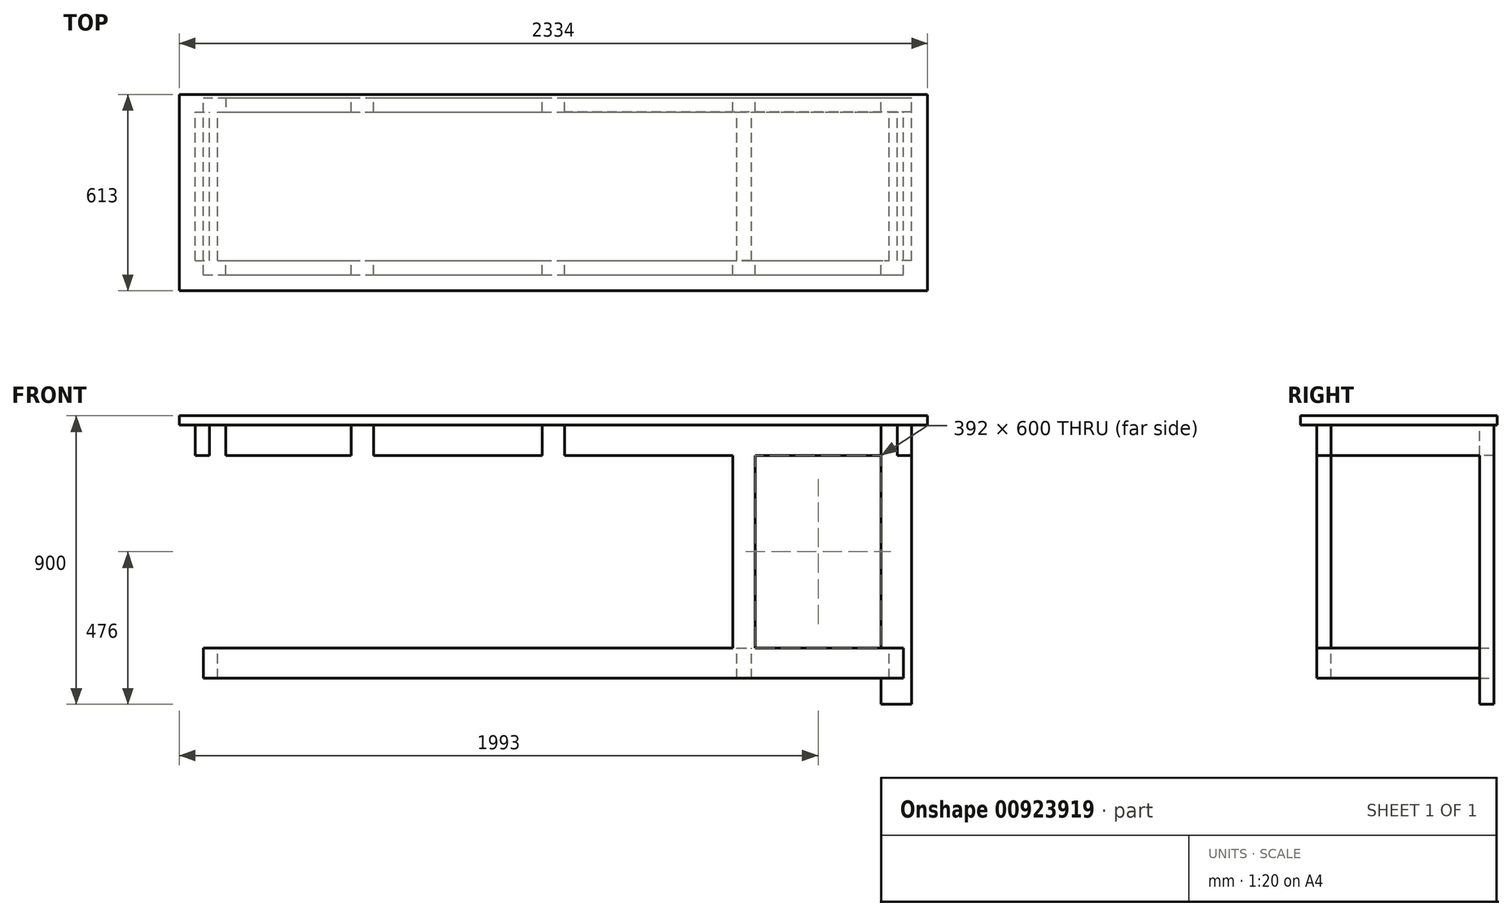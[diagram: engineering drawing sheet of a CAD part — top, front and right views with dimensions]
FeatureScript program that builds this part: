
annotation { "Feature Type Name" : "Feature", "Feature Type Description" : "" }
export const myFeature = defineFeature(function(context is Context, id is Id, definition is map)
    precondition{}
    {
        {
            var Q0;
            Q0=qCreatedBy(makeId("Top.planeOp"),FACE);
            cPlane(context, id + "F0", {"entities" : qUnion([Q0]), "cplaneType" : CPlaneType.OFFSET, "offset" : 900 * mm, "width" : 150 * mm, "height" : 150 * mm});
        }
        {
            var Q0;
            Q0=qCreatedBy(id+"F0.planeOp",FACE);
            var sketch = newSketch(context, id + "F1", { "sketchPlane" : qUnion([Q0])});
            skLineSegment(sketch, "E0.bottom", {"start": v(1167, -306.5) * mm, "end": v(-1167, -306.5) * mm});
            skLineSegment(sketch, "E0.top", {"start": v(1167, 306.5) * mm, "end": v(-1167, 306.5) * mm});
            skLineSegment(sketch, "E0.left", {"start": v(1167, -306.5) * mm, "end": v(1167, 306.5) * mm});
            skLineSegment(sketch, "E0.right", {"start": v(-1167, -306.5) * mm, "end": v(-1167, 306.5) * mm});
            skPoint(sketch, "E0.middle", {"position": v(0, 0) * mm});
            skSolve(sketch);
        }
        {
            var Q0;
            Q0=makeQuery(id+"F1.imprint","IMPRINT",FACE,{"disambiguationData":[TD([[makeQuery(id+"F1.imprint","IMPRINT",EDGE,{"derivedFrom":sQuery(id+"F1.wireOp",EDGE,"E0.bottom")}),-1.0]])]});
            extrude(context, id + "F2", {"entities" : qUnion([Q0]), "oppositeDirection" : true, "depth" : 29 * mm, "offsetDistance" : 25 * mm});
        }
        {
            var Q0;
            Q0=makeQuery(id+"F2.opExtrude","CAP_FACE",FACE,{"disambiguationData":[OSD([sQuery(id+"F1.wireOp",EDGE,"E0.bottom"),sQuery(id+"F1.wireOp",EDGE,"E0.top"),sQuery(id+"F1.wireOp",EDGE,"E0.left"),sQuery(id+"F1.wireOp",EDGE,"E0.right")])],"isStart":false});
            var sketch = newSketch(context, id + "F3", { "sketchPlane" : qUnion([Q0])});
            skLineSegment(sketch, "E1", {"start": v(0, -352.14) * mm, "end": v(0, 338.4) * mm, "construction": true});
            skPoint(sketch, "E1.endSnap0", {"position": v(0, 306.5) * mm});
            skLineSegment(sketch, "E2", {"start": v(-1212.18, 0) * mm, "end": v(1197.3, 0) * mm, "construction": true});
            skLineSegment(sketch, "E3.bottom", {"start": v(-1117, 256.5) * mm, "end": v(1117, 256.5) * mm});
            skLineSegment(sketch, "E3.top", {"start": v(-1117, -296.5) * mm, "end": v(1117, -296.5) * mm});
            skLineSegment(sketch, "E3.left", {"start": v(-1117, 256.5) * mm, "end": v(-1117, -296.5) * mm});
            skLineSegment(sketch, "E3.right", {"start": v(1117, 256.5) * mm, "end": v(1117, -296.5) * mm});
            skLineSegment(sketch, "E4.bottom", {"start": v(-1072, 211.5) * mm, "end": v(1072, 211.5) * mm});
            skLineSegment(sketch, "E4.top", {"start": v(-1072, -251.5) * mm, "end": v(1072, -251.5) * mm});
            skLineSegment(sketch, "E4.left", {"start": v(-1072, 211.5) * mm, "end": v(-1072, -251.5) * mm});
            skLineSegment(sketch, "E4.right", {"start": v(1072, 211.5) * mm, "end": v(1072, -251.5) * mm});
            skLineSegment(sketch, "E5.bottom", {"start": v(-22.5, 211.5) * mm, "end": v(22.5, 211.5) * mm});
            skLineSegment(sketch, "E5.top", {"start": v(-22.5, -251.5) * mm, "end": v(22.5, -251.5) * mm});
            skLineSegment(sketch, "E5.left", {"start": v(-22.5, 211.5) * mm, "end": v(-22.5, -251.5) * mm});
            skLineSegment(sketch, "E5.right", {"start": v(22.5, 211.5) * mm, "end": v(22.5, -251.5) * mm});
            skLineSegment(sketch, "E6.bottom", {"start": v(-1117, 256.5) * mm, "end": v(-1022, 256.5) * mm});
            skLineSegment(sketch, "E6.top", {"start": v(-1117, 211.5) * mm, "end": v(-1022, 211.5) * mm});
            skLineSegment(sketch, "E6.left", {"start": v(-1117, 256.5) * mm, "end": v(-1117, 211.5) * mm});
            skLineSegment(sketch, "E6.right", {"start": v(-1022, 256.5) * mm, "end": v(-1022, 211.5) * mm});
            skLineSegment(sketch, "E7.bottom", {"start": v(-35, 256.5) * mm, "end": v(35, 256.5) * mm});
            skLineSegment(sketch, "E7.top", {"start": v(-35, 211.5) * mm, "end": v(35, 211.5) * mm});
            skLineSegment(sketch, "E7.left", {"start": v(-35, 256.5) * mm, "end": v(-35, 211.5) * mm});
            skLineSegment(sketch, "E7.right", {"start": v(35, 256.5) * mm, "end": v(35, 211.5) * mm});
            skLineSegment(sketch, "E8.bottom", {"start": v(-1117, -296.5) * mm, "end": v(-1022, -296.5) * mm});
            skLineSegment(sketch, "E8.top", {"start": v(-1117, -251.5) * mm, "end": v(-1022, -251.5) * mm});
            skLineSegment(sketch, "E8.left", {"start": v(-1117, -296.5) * mm, "end": v(-1117, -251.5) * mm});
            skLineSegment(sketch, "E8.right", {"start": v(-1022, -296.5) * mm, "end": v(-1022, -251.5) * mm});
            skLineSegment(sketch, "E9.MirrorCS", {"start": v(1022, -296.5) * mm, "end": v(1022, -251.5) * mm});
            skLineSegment(sketch, "E10.MirrorCS", {"start": v(1117, -251.5) * mm, "end": v(1022, -251.5) * mm});
            skLineSegment(sketch, "E11.MirrorCS", {"start": v(1117, -296.5) * mm, "end": v(1022, -296.5) * mm});
            skLineSegment(sketch, "E12.MirrorCS", {"start": v(1117, 211.5) * mm, "end": v(1022, 211.5) * mm});
            skLineSegment(sketch, "E13.MirrorCS", {"start": v(1117, 256.5) * mm, "end": v(1022, 256.5) * mm});
            skLineSegment(sketch, "E14.MirrorCS", {"start": v(1022, 256.5) * mm, "end": v(1022, 211.5) * mm});
            skLineSegment(sketch, "E15.MirrorCS", {"start": v(1117, 256.5) * mm, "end": v(1117, 211.5) * mm});
            skLineSegment(sketch, "E16.bottom", {"start": v(-35, -251.5) * mm, "end": v(35, -251.5) * mm});
            skLineSegment(sketch, "E16.top", {"start": v(-35, -296.5) * mm, "end": v(35, -296.5) * mm});
            skLineSegment(sketch, "E16.left", {"start": v(-35, -251.5) * mm, "end": v(-35, -296.5) * mm});
            skLineSegment(sketch, "E16.right", {"start": v(35, -251.5) * mm, "end": v(35, -296.5) * mm});
            skLineSegment(sketch, "E17.bottom", {"start": v(-630, 256.5) * mm, "end": v(-560, 256.5) * mm});
            skLineSegment(sketch, "E17.top", {"start": v(-630, 211.5) * mm, "end": v(-560, 211.5) * mm});
            skLineSegment(sketch, "E17.left", {"start": v(-630, 256.5) * mm, "end": v(-630, 211.5) * mm});
            skLineSegment(sketch, "E17.right", {"start": v(-560, 256.5) * mm, "end": v(-560, 211.5) * mm});
            skLineSegment(sketch, "E18.bottom", {"start": v(-630, -251.5) * mm, "end": v(-560, -251.5) * mm});
            skLineSegment(sketch, "E18.top", {"start": v(-630, -296.5) * mm, "end": v(-560, -296.5) * mm});
            skLineSegment(sketch, "E18.left", {"start": v(-630, -251.5) * mm, "end": v(-630, -296.5) * mm});
            skLineSegment(sketch, "E18.right", {"start": v(-560, -251.5) * mm, "end": v(-560, -296.5) * mm});
            skLineSegment(sketch, "E19.MirrorCS", {"start": v(630, 256.5) * mm, "end": v(630, 211.5) * mm});
            skLineSegment(sketch, "E20.MirrorCS", {"start": v(630, 256.5) * mm, "end": v(560, 256.5) * mm});
            skLineSegment(sketch, "E21.MirrorCS", {"start": v(560, 256.5) * mm, "end": v(560, 211.5) * mm});
            skLineSegment(sketch, "E22.MirrorCS", {"start": v(630, 211.5) * mm, "end": v(560, 211.5) * mm});
            skLineSegment(sketch, "E23.MirrorCS", {"start": v(630, -251.5) * mm, "end": v(630, -296.5) * mm});
            skLineSegment(sketch, "E24.MirrorCS", {"start": v(630, -296.5) * mm, "end": v(560, -296.5) * mm});
            skLineSegment(sketch, "E25.MirrorCS", {"start": v(560, -251.5) * mm, "end": v(560, -296.5) * mm});
            skSolve(sketch);
        }
        {
            var Q0;
            Q0=makeQuery(id+"F3.imprint","IMPRINT",FACE,{"disambiguationData":[TD([[makeQuery(id+"F3.imprint","IMPRINT",EDGE,{"derivedFrom":sQuery(id+"F3.wireOp",EDGE,"E6.bottom")}),-1.0]])]});
            var Q1;
            Q1=makeQuery(id+"F3.imprint","IMPRINT",FACE,{"disambiguationData":[TD([[makeQuery(id+"F3.imprint","IMPRINT",EDGE,{"derivedFrom":sQuery(id+"F3.wireOp",EDGE,"E8.bottom")}),1.0]])]});
            var Q2;
            {var subQ1=sQuery(id+"F3.wireOp",EDGE,"E9.MirrorCS");Q2=makeQuery(id+"F3.imprint","IMPRINT",FACE,{"disambiguationData":[TD([[makeQuery(id+"F3.imprint","IMPRINT",EDGE,{"derivedFrom":subQ1}),-1.0]])]});}
            var Q3;
            Q3=makeQuery(id+"F3.imprint","IMPRINT",FACE,{"disambiguationData":[TD([[makeQuery(id+"F3.imprint","IMPRINT",EDGE,{"derivedFrom":sQuery(id+"F3.wireOp",EDGE,"E13.MirrorCS")}),1.0]])]});
            var Q4;
            Q4=makeQuery(id+"F3.imprint","IMPRINT",FACE,{"disambiguationData":[TD([[makeQuery(id+"F3.imprint","IMPRINT",EDGE,{"derivedFrom":sQuery(id+"F3.wireOp",EDGE,"E7.bottom")}),-1.0]])]});
            var Q5;
            Q5=makeQuery(id+"F3.imprint","IMPRINT",FACE,{"disambiguationData":[TD([[makeQuery(id+"F3.imprint","IMPRINT",EDGE,{"derivedFrom":sQuery(id+"F3.wireOp",EDGE,"E16.top")}),1.0]])]});
            extrude(context, id + "F4", {"entities" : qUnion([Q0, Q1, Q2, Q3, Q4, Q5]), "operationType" : NewBodyOperationType.ADD, "depth" : (900 - 29) * mm, "offsetDistance" : 25 * mm});
        }
        {
            var Q0;
            Q0=qCreatedBy(makeId("Top.planeOp"),FACE);
            cPlane(context, id + "F5", {"entities" : qUnion([Q0]), "cplaneType" : CPlaneType.OFFSET, "offset" : 176 * mm, "width" : 150 * mm, "height" : 150 * mm});
        }
        {
            var Q0;
            Q0=qCreatedBy(id+"F5.planeOp",FACE);
            var sketch = newSketch(context, id + "F6", { "sketchPlane" : qUnion([Q0])});
            skLineSegment(sketch, "E26", {"start": v(0, -296.69) * mm, "end": v(0, 323.31) * mm, "construction": true});
            skLineSegment(sketch, "E27", {"start": v(-1009.8, 0) * mm, "end": v(1031.2, 0) * mm, "construction": true});
            skLineSegment(sketch, "E28.bottom", {"start": v(-1092, -256.5) * mm, "end": v(1092, -256.5) * mm});
            skLineSegment(sketch, "E28.top", {"start": v(-1092, 296.5) * mm, "end": v(1092, 296.5) * mm});
            skLineSegment(sketch, "E28.left", {"start": v(-1092, -256.5) * mm, "end": v(-1092, 296.5) * mm});
            skLineSegment(sketch, "E28.right", {"start": v(1092, -256.5) * mm, "end": v(1092, 296.5) * mm});
            skLineSegment(sketch, "E29.bottom", {"start": v(-1047, -211.5) * mm, "end": v(1047, -211.5) * mm});
            skLineSegment(sketch, "E29.top", {"start": v(-1047, 251.5) * mm, "end": v(1047, 251.5) * mm});
            skLineSegment(sketch, "E29.left", {"start": v(-1047, -211.5) * mm, "end": v(-1047, 251.5) * mm});
            skLineSegment(sketch, "E29.right", {"start": v(1047, -211.5) * mm, "end": v(1047, 251.5) * mm});
            skLineSegment(sketch, "E30.bottom", {"start": v(-22.5, -211.5) * mm, "end": v(22.5, -211.5) * mm});
            skLineSegment(sketch, "E30.top", {"start": v(-22.5, 251.5) * mm, "end": v(22.5, 251.5) * mm});
            skLineSegment(sketch, "E30.left", {"start": v(-22.5, -211.5) * mm, "end": v(-22.5, 251.5) * mm});
            skLineSegment(sketch, "E30.right", {"start": v(22.5, -211.5) * mm, "end": v(22.5, 251.5) * mm});
            skLineSegment(sketch, "E31.bottom", {"start": v(-617.5, -211.5) * mm, "end": v(-572.5, -211.5) * mm});
            skLineSegment(sketch, "E31.top", {"start": v(-617.5, 251.5) * mm, "end": v(-572.5, 251.5) * mm});
            skLineSegment(sketch, "E31.left", {"start": v(-617.5, -211.5) * mm, "end": v(-617.5, 251.5) * mm});
            skLineSegment(sketch, "E31.right", {"start": v(-572.5, -211.5) * mm, "end": v(-572.5, 251.5) * mm});
            skLineSegment(sketch, "E32.MirrorCS", {"start": v(572.5, -211.5) * mm, "end": v(572.5, 251.5) * mm});
            skLineSegment(sketch, "E33.MirrorCS", {"start": v(617.5, -211.5) * mm, "end": v(617.5, 251.5) * mm});
            skLineSegment(sketch, "E34.MirrorCS", {"start": v(617.5, 251.5) * mm, "end": v(572.5, 251.5) * mm});
            skSolve(sketch);
        }
        {
            var Q0;
            {var subQ0=sQuery(id+"F3.wireOp",EDGE,"E3.left");Q0=makeQuery(id+"F3.imprint","IMPRINT",FACE,{"disambiguationData":[TD([[makeQuery(id+"F3.imprint","IMPRINT",EDGE,{"derivedFrom":subQ0}),1.0]])]});}
            var Q1;
            {var subQ0=sQuery(id+"F3.wireOp",EDGE,"E6.right");Q1=makeQuery(id+"F3.imprint","IMPRINT",FACE,{"disambiguationData":[TD([[makeQuery(id+"F3.imprint","IMPRINT",EDGE,{"derivedFrom":subQ0}),1.0]])]});}
            var Q2;
            {var subQ0=sQuery(id+"F3.wireOp",EDGE,"E8.right");Q2=makeQuery(id+"F3.imprint","IMPRINT",FACE,{"disambiguationData":[TD([[makeQuery(id+"F3.imprint","IMPRINT",EDGE,{"derivedFrom":subQ0}),-1.0]])]});}
            var Q3;
            {var subQ0=sQuery(id+"F3.wireOp",EDGE,"E16.left");Q3=makeQuery(id+"F3.imprint","IMPRINT",FACE,{"disambiguationData":[TD([[makeQuery(id+"F3.imprint","IMPRINT",EDGE,{"derivedFrom":subQ0}),-1.0]])]});}
            var Q4;
            {var subQ0=sQuery(id+"F3.wireOp",EDGE,"E7.left");Q4=makeQuery(id+"F3.imprint","IMPRINT",FACE,{"disambiguationData":[TD([[makeQuery(id+"F3.imprint","IMPRINT",EDGE,{"derivedFrom":subQ0}),-1.0]])]});}
            var Q5;
            {var subQ0=sQuery(id+"F3.wireOp",EDGE,"E7.right");Q5=makeQuery(id+"F3.imprint","IMPRINT",FACE,{"disambiguationData":[TD([[makeQuery(id+"F3.imprint","IMPRINT",EDGE,{"derivedFrom":subQ0}),1.0]])]});}
            var Q6;
            {var subQ0=sQuery(id+"F3.wireOp",EDGE,"E16.right");Q6=makeQuery(id+"F3.imprint","IMPRINT",FACE,{"disambiguationData":[TD([[makeQuery(id+"F3.imprint","IMPRINT",EDGE,{"derivedFrom":subQ0}),1.0]])]});}
            var Q7;
            {var subQ0=sQuery(id+"F3.wireOp",EDGE,"E9.MirrorCS");Q7=makeQuery(id+"F3.imprint","IMPRINT",FACE,{"disambiguationData":[TD([[makeQuery(id+"F3.imprint","IMPRINT",EDGE,{"derivedFrom":subQ0}),1.0]])]});}
            var Q8;
            {var subQ0=sQuery(id+"F3.wireOp",EDGE,"E14.MirrorCS");Q8=makeQuery(id+"F3.imprint","IMPRINT",FACE,{"disambiguationData":[TD([[makeQuery(id+"F3.imprint","IMPRINT",EDGE,{"derivedFrom":subQ0}),-1.0]])]});}
            var Q9;
            {var subQ5=sQuery(id+"F3.wireOp",EDGE,"E4.right");Q9=makeQuery(id+"F3.imprint","IMPRINT",FACE,{"disambiguationData":[TD([[makeQuery(id+"F3.imprint","IMPRINT",EDGE,{"derivedFrom":subQ5}),1.0]])]});}
            extrude(context, id + "F7", {"entities" : qUnion([Q0, Q1, Q2, Q3, Q4, Q5, Q6, Q7, Q8, Q9]), "operationType" : NewBodyOperationType.ADD, "depth" : 95 * mm, "offsetDistance" : 25 * mm});
        }
        {
            var Q0;
            Q0=makeQuery(id+"F3.imprint","IMPRINT",FACE,{"disambiguationData":[TD([[makeQuery(id+"F3.imprint","IMPRINT",EDGE,{"derivedFrom":sQuery(id+"F3.wireOp",EDGE,"E17.bottom")}),-1.0]])]});
            var Q1;
            Q1=makeQuery(id+"F3.imprint","IMPRINT",FACE,{"disambiguationData":[TD([[makeQuery(id+"F3.imprint","IMPRINT",EDGE,{"derivedFrom":sQuery(id+"F3.wireOp",EDGE,"E18.bottom")}),-1.0]])]});
            var Q2;
            {var subQ0=sQuery(id+"F3.wireOp",EDGE,"E23.MirrorCS");Q2=makeQuery(id+"F3.imprint","IMPRINT",FACE,{"disambiguationData":[TD([[makeQuery(id+"F3.imprint","IMPRINT",EDGE,{"derivedFrom":subQ0}),-1.0]])]});}
            var Q3;
            Q3=makeQuery(id+"F3.imprint","IMPRINT",FACE,{"disambiguationData":[TD([[makeQuery(id+"F3.imprint","IMPRINT",EDGE,{"derivedFrom":sQuery(id+"F3.wireOp",EDGE,"E19.MirrorCS")}),-1.0]])]});
            extrude(context, id + "F8", {"entities" : qUnion([Q0, Q1, Q2, Q3]), "operationType" : NewBodyOperationType.ADD, "depth" : 750 * mm, "offsetDistance" : 25 * mm});
        }
        {
            var Q0;
            Q0=makeQuery(id+"F6.imprint","IMPRINT",FACE,{"disambiguationData":[TD([[makeQuery(id+"F6.imprint","IMPRINT",EDGE,{"derivedFrom":sQuery(id+"F6.wireOp",EDGE,"E28.bottom")}),1.0]])]});
            var Q1;
            Q1=makeQuery(id+"F6.imprint","IMPRINT",FACE,{"disambiguationData":[TD([[makeQuery(id+"F6.imprint","IMPRINT",EDGE,{"derivedFrom":sQuery(id+"F6.wireOp",EDGE,"E31.bottom")}),1.0]])]});
            var Q2;
            Q2=makeQuery(id+"F6.imprint","IMPRINT",FACE,{"disambiguationData":[TD([[makeQuery(id+"F6.imprint","IMPRINT",EDGE,{"derivedFrom":sQuery(id+"F6.wireOp",EDGE,"E30.bottom")}),1.0]])]});
            var Q3;
            {var subQ0=sQuery(id+"F6.wireOp",EDGE,"E32.MirrorCS");Q3=makeQuery(id+"F6.imprint","IMPRINT",FACE,{"disambiguationData":[TD([[makeQuery(id+"F6.imprint","IMPRINT",EDGE,{"derivedFrom":subQ0}),-1.0]])]});}
            extrude(context, id + "F9", {"entities" : qUnion([Q0, Q1, Q2, Q3]), "operationType" : NewBodyOperationType.ADD, "depth" : -95 * mm, "offsetDistance" : 25 * mm});
        }
        {
            var Q0;
            Q0=qCreatedBy(makeId("Top.planeOp"),FACE);
            cPlane(context, id + "F10", {"entities" : qUnion([Q0]), "cplaneType" : CPlaneType.OFFSET, "offset" : 356 * mm, "width" : 150 * mm, "height" : 150 * mm});
        }
    });
